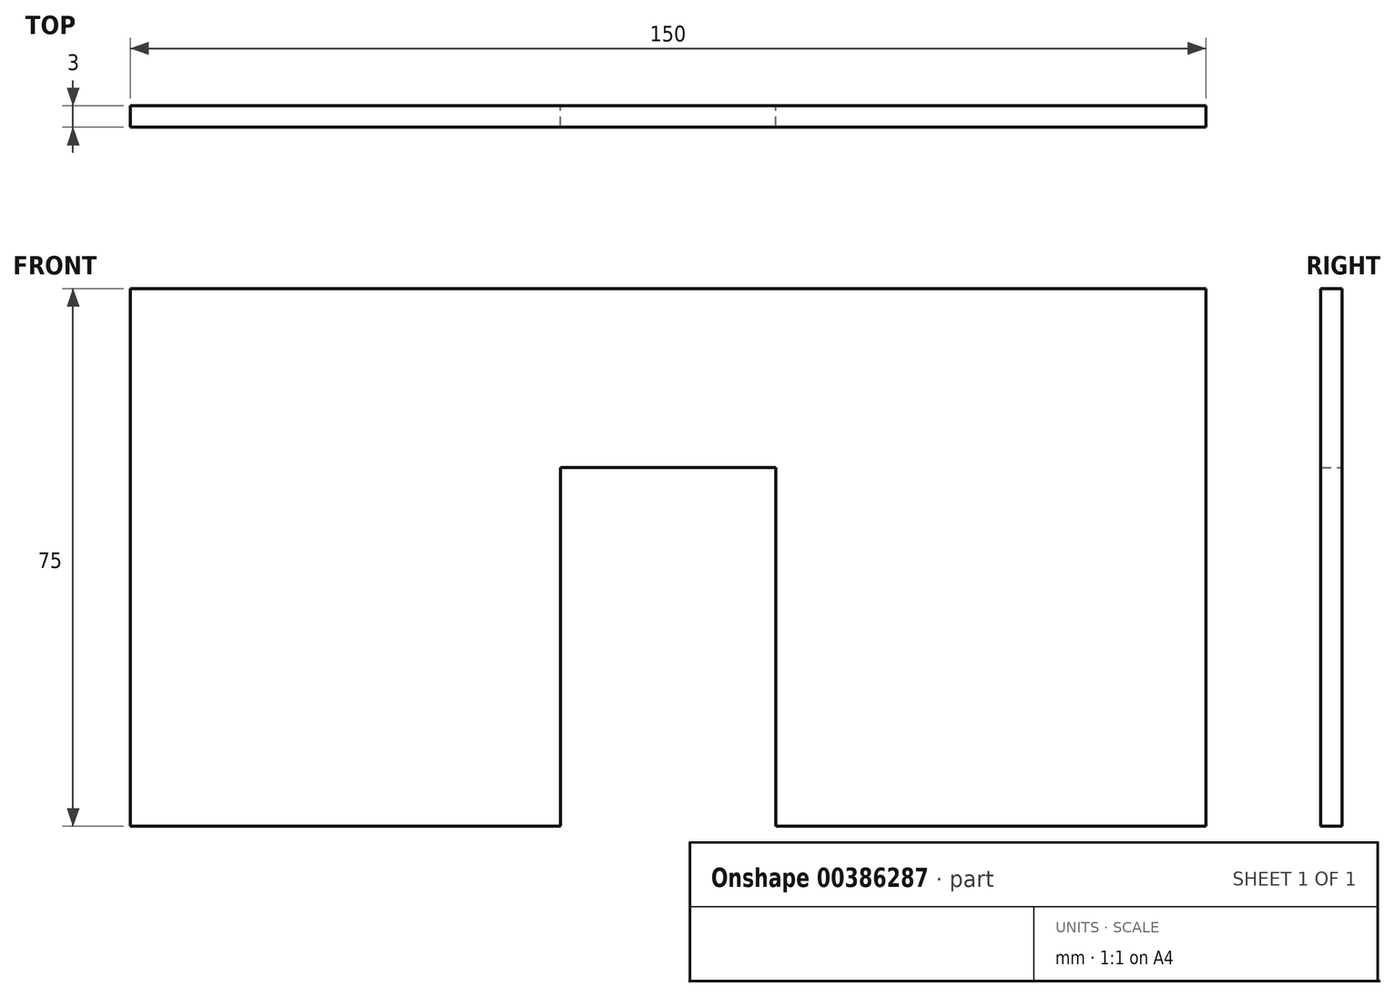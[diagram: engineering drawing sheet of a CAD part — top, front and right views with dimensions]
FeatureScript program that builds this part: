
annotation { "Feature Type Name" : "Feature", "Feature Type Description" : "" }
export const myFeature = defineFeature(function(context is Context, id is Id, definition is map)
    precondition{}
    {
        {
            var Q0;
            Q0=qCreatedBy(makeId("Front.planeOp"),FACE);
            var sketch = newSketch(context, id + "F0", { "sketchPlane" : qUnion([Q0])});
            skLineSegment(sketch, "E0.bottom", {"start": v(-60, 75) * mm, "end": v(90, 75) * mm});
            skLineSegment(sketch, "E0.top", {"start": v(-60, 0) * mm, "end": v(90, 0) * mm});
            skLineSegment(sketch, "E0.left", {"start": v(-60, 75) * mm, "end": v(-60, 0) * mm});
            skLineSegment(sketch, "E0.right", {"start": v(90, 75) * mm, "end": v(90, 0) * mm});
            skLineSegment(sketch, "E1.bottom", {"start": v(0, 50) * mm, "end": v(30, 50) * mm});
            skLineSegment(sketch, "E1.top", {"start": v(0, 0) * mm, "end": v(30, 0) * mm});
            skLineSegment(sketch, "E1.left", {"start": v(0, 50) * mm, "end": v(0, 0) * mm});
            skLineSegment(sketch, "E1.right", {"start": v(30, 50) * mm, "end": v(30, 0) * mm});
            skSolve(sketch);
        }
        {
            var Q0;
            Q0=makeQuery(id+"F0.imprint","IMPRINT",FACE,{"disambiguationData":[TD([[makeQuery(id+"F0.imprint","IMPRINT",EDGE,{"derivedFrom":sQuery(id+"F0.wireOp",EDGE,"E0.bottom")}),-1.0]])]});
            extrude(context, id + "F1", {"entities" : qUnion([Q0]), "depth" : 3 * mm});
        }
    });
